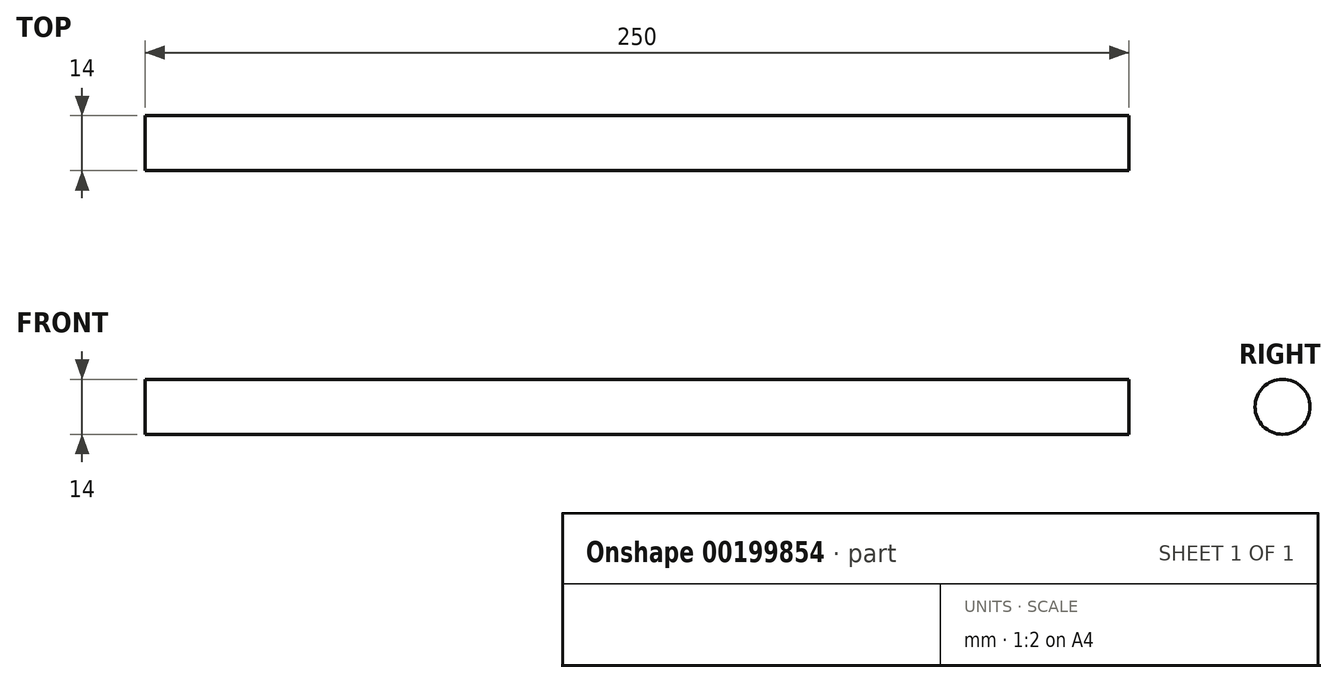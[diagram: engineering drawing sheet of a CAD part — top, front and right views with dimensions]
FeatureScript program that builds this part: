
annotation { "Feature Type Name" : "Feature", "Feature Type Description" : "" }
export const myFeature = defineFeature(function(context is Context, id is Id, definition is map)
    precondition{}
    {
        {
            var Q0;
            Q0=qCreatedBy(makeId("Right.planeOp"),FACE);
            var sketch = newSketch(context, id + "F0", { "sketchPlane" : qUnion([Q0])});
            skCircle(sketch, "E0", {"center": v(0, 0) * mm, "radius": 7 * mm});
            skSolve(sketch);
        }
        {
            var Q0;
            Q0=makeQuery(id+"F0.imprint","IMPRINT",FACE,{"disambiguationData":[TD([[makeQuery(id+"F0.imprint","IMPRINT",EDGE,{"derivedFrom":sQuery(id+"F0.wireOp",EDGE,"E0")}),1.0]])]});
            extrude(context, id + "F1", {"entities" : qUnion([Q0]), "endBound" : BoundingType.SYMMETRIC, "depth" : 250 * mm});
        }
    });
